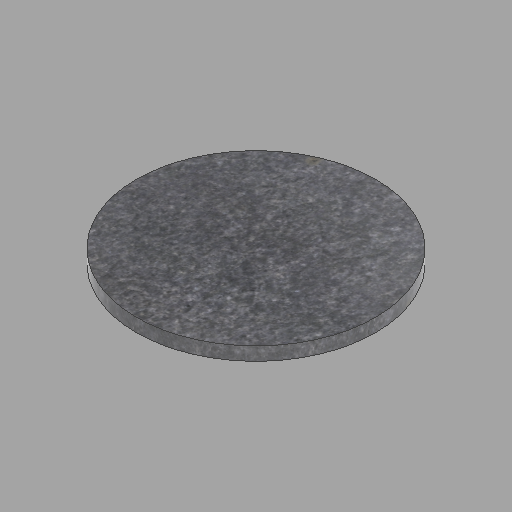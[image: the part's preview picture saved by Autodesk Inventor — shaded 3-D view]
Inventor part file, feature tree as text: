
AUTODESK INVENTOR PART (.ipt)
format: ipt  version: 2023 (Build 270158000, 158)  size: 218,624 bytes
history: native  units: in
note: dims shown in document units (in); Inventor stores cm internally (conversion verified against a paired STEP export)
features: extrude x2, sketch x2, other x1, projected_geometry x1
ambient origin geometry x8: Origin, YZ Plane, XZ Plane, XY Plane, X Axis, Y Axis, Z Axis, Center Point
bodies: Solid1 (feature_tree)
feature tree (6):
  other  "2x36x36-1"
  extrude  "Extrusion1"  Depth=36.0in
  extrude  "Extrusion2"  TaperAngle=0.0deg  [1 undecoded]
  sketch  "Sketch1"  dims[d0=2.0in d1=36.0in]
  sketch  "Sketch2"  dims[d2=36.0in d3=0.0in d4=0.0in d5=0.0in]
  projected_geometry  "Projected Loop1"
note: 1 required parameter value undecoded (feature->parameter linkage not recoverable at this tier; creation-order binding heuristic only, values carry confidence <= 0.55)
